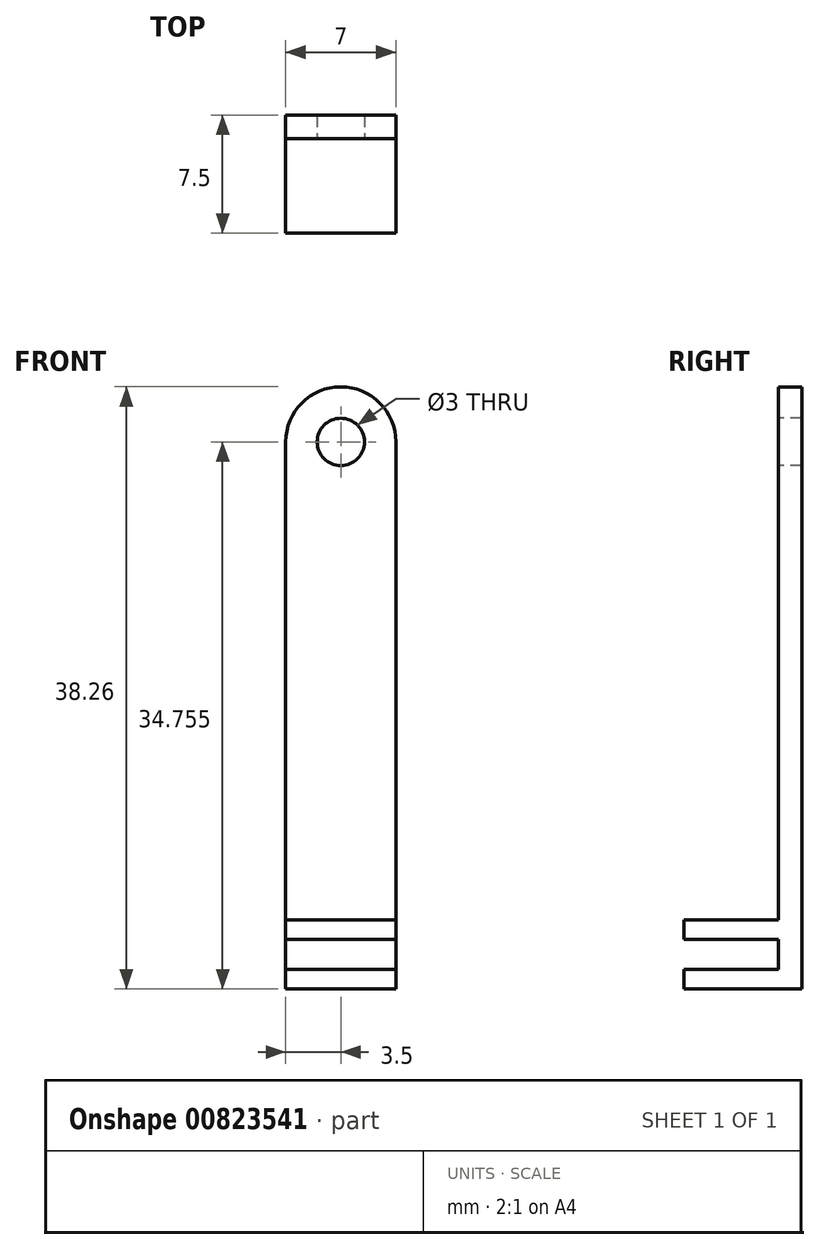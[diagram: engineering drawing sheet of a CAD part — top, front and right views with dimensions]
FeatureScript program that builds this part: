
annotation { "Feature Type Name" : "Feature", "Feature Type Description" : "" }
export const myFeature = defineFeature(function(context is Context, id is Id, definition is map)
    precondition{}
    {
        {
            var Q0;
            Q0=qCreatedBy(makeId("Front.planeOp"),FACE);
            var sketch = newSketch(context, id + "F0", { "sketchPlane" : qUnion([Q0])});
            skLineSegment(sketch, "E0.bottom", {"start": v(-3.5, 17.38) * mm, "end": v(3.5, 17.38) * mm});
            skLineSegment(sketch, "E0.top", {"start": v(-3.5, -17.38) * mm, "end": v(3.5, -17.38) * mm});
            skLineSegment(sketch, "E0.left", {"start": v(-3.5, 17.38) * mm, "end": v(-3.5, -17.38) * mm});
            skLineSegment(sketch, "E0.right", {"start": v(3.5, 17.38) * mm, "end": v(3.5, -17.38) * mm});
            skPoint(sketch, "E0.middle", {"position": v(0, 0) * mm});
            skArc(sketch, "E1", {"start": v(3.5, 17.38) * mm, "mid": v(0, 20.88) * mm, "end": v(-3.5, 17.38) * mm});
            skCircle(sketch, "E2", {"center": v(0, 17.38) * mm, "radius": 1.5 * mm});
            skLineSegment(sketch, "E3.top", {"start": v(-3.5, -16.12) * mm, "end": v(3.5, -16.12) * mm});
            skLineSegment(sketch, "E3.left", {"start": v(-3.5, -17.38) * mm, "end": v(-3.5, -16.12) * mm});
            skLineSegment(sketch, "E3.right", {"start": v(3.5, -17.38) * mm, "end": v(3.5, -16.12) * mm});
            skLineSegment(sketch, "E4.bottom", {"start": v(-3.5, -14.22) * mm, "end": v(3.5, -14.22) * mm});
            skLineSegment(sketch, "E4.top", {"start": v(-3.5, -12.97) * mm, "end": v(3.5, -12.97) * mm});
            skLineSegment(sketch, "E4.left", {"start": v(-3.5, -14.23) * mm, "end": v(-3.5, -12.97) * mm});
            skLineSegment(sketch, "E4.right", {"start": v(3.5, -14.22) * mm, "end": v(3.5, -12.97) * mm});
            skSolve(sketch);
        }
        {
            var Q0;
            {var subQ1=sQuery(id+"F0.wireOp",EDGE,"E0.left");Q0=makeQuery(id+"F0.imprint","IMPRINT",FACE,{"disambiguationData":[TD([[makeQuery(id+"F0.imprint","IMPRINT",EDGE,{"derivedFrom":subQ1}),1.0]])]});}
            var Q1;
            Q1=makeQuery(id+"F0.imprint","IMPRINT",FACE,{"disambiguationData":[TD([[makeQuery(id+"F0.imprint","IMPRINT",EDGE,{"derivedFrom":sQuery(id+"F0.wireOp",EDGE,"E0.top")}),1.0]])]});
            var Q2;
            {var subQ0=sQuery(id+"F0.wireOp",EDGE,"E1");Q2=makeQuery(id+"F0.imprint","IMPRINT",FACE,{"disambiguationData":[TD([[makeQuery(id+"F0.imprint","IMPRINT",EDGE,{"derivedFrom":subQ0}),1.0]])]});}
            var Q3;
            Q3=makeQuery(id+"F0.imprint","IMPRINT",FACE,{"disambiguationData":[TD([[makeQuery(id+"F0.imprint","IMPRINT",EDGE,{"derivedFrom":sQuery(id+"F0.wireOp",EDGE,"E4.bottom")}),1.0]])]});
            var Q4;
            {var subQ4=sQuery(id+"F0.wireOp",EDGE,"E4.top");Q4=makeQuery(id+"F0.imprint","IMPRINT",FACE,{"disambiguationData":[TD([[makeQuery(id+"F0.imprint","IMPRINT",EDGE,{"derivedFrom":subQ4}),1.0]])]});}
            extrude(context, id + "F1", {"entities" : qUnion([Q0, Q1, Q2, Q3, Q4]), "oppositeDirection" : true, "depth" : 1.5 * mm, "offsetDistance" : 25 * mm});
        }
        {
            var Q0;
            Q0=makeQuery(id+"F0.imprint","IMPRINT",FACE,{"disambiguationData":[TD([[makeQuery(id+"F0.imprint","IMPRINT",EDGE,{"derivedFrom":sQuery(id+"F0.wireOp",EDGE,"E0.top")}),1.0]])]});
            var Q1;
            Q1=makeQuery(id+"F0.imprint","IMPRINT",FACE,{"disambiguationData":[TD([[makeQuery(id+"F0.imprint","IMPRINT",EDGE,{"derivedFrom":sQuery(id+"F0.wireOp",EDGE,"E4.bottom")}),1.0]])]});
            extrude(context, id + "F2", {"entities" : qUnion([Q0, Q1]), "operationType" : NewBodyOperationType.ADD, "depth" : 6 * mm, "offsetDistance" : 25 * mm});
        }
    });
